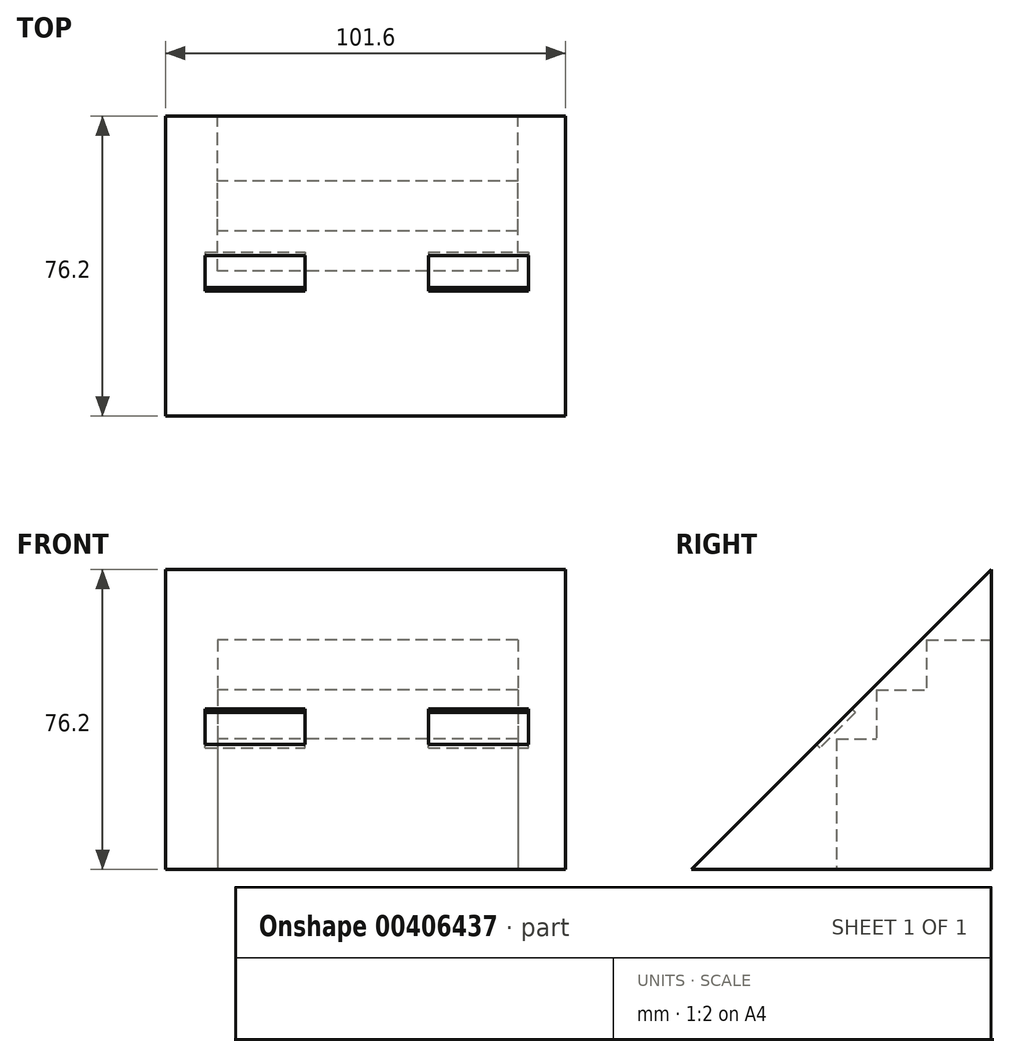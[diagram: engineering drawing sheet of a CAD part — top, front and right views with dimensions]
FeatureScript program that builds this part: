
annotation { "Feature Type Name" : "Feature", "Feature Type Description" : "" }
export const myFeature = defineFeature(function(context is Context, id is Id, definition is map)
    precondition{}
    {
        {
            var Q0;
            Q0=qCreatedBy(makeId("Right.planeOp"),FACE);
            var sketch = newSketch(context, id + "F0", { "sketchPlane" : qUnion([Q0])});
            skLineSegment(sketch, "E0.top", {"start": v(-48.38, -33.15) * mm, "end": v(27.82, -33.15) * mm});
            skLineSegment(sketch, "E0.right", {"start": v(27.82, 43.05) * mm, "end": v(27.82, -33.15) * mm});
            skLineSegment(sketch, "E1", {"start": v(27.82, 43.05) * mm, "end": v(-48.38, -33.15) * mm});
            skSolve(sketch);
        }
        {
            var Q0;
            Q0=makeQuery(id+"F0.imprint","IMPRINT",FACE,{"disambiguationData":[TD([[makeQuery(id+"F0.imprint","IMPRINT",EDGE,{"derivedFrom":sQuery(id+"F0.wireOp",EDGE,"E0.top")}),1.0]])]});
            extrude(context, id + "F1", {"entities" : qUnion([Q0]), "depth" : 101.6 * mm});
        }
        {
            var Q0;
            Q0=makeQuery(id+"F1.opExtrude","SWEPT_FACE",FACE,{"disambiguationData":[OSD([sQuery(id+"F0.wireOp",EDGE,"E1")])]});
            var sketch = newSketch(context, id + "F2", { "sketchPlane" : qUnion([Q0])});
            skLineSegment(sketch, "E2.bottom", {"start": v(10, 0) * mm, "end": v(35.4, 0) * mm});
            skLineSegment(sketch, "E2.top", {"start": v(10, -12.7) * mm, "end": v(35.4, -12.7) * mm});
            skLineSegment(sketch, "E2.left", {"start": v(10, 0) * mm, "end": v(10, -12.7) * mm});
            skLineSegment(sketch, "E2.right", {"start": v(35.4, 0) * mm, "end": v(35.4, -12.7) * mm});
            skLineSegment(sketch, "E3.bottom", {"start": v(66.77, 0) * mm, "end": v(92.17, 0) * mm});
            skLineSegment(sketch, "E3.top", {"start": v(66.77, -12.7) * mm, "end": v(92.17, -12.7) * mm});
            skLineSegment(sketch, "E3.left", {"start": v(66.77, 0) * mm, "end": v(66.77, -12.7) * mm});
            skLineSegment(sketch, "E3.right", {"start": v(92.17, 0) * mm, "end": v(92.17, -12.7) * mm});
            skSolve(sketch);
        }
        {
            var Q0;
            Q0=makeQuery(id+"F2.imprint","IMPRINT",FACE,{"disambiguationData":[TD([[makeQuery(id+"F2.imprint","IMPRINT",EDGE,{"derivedFrom":sQuery(id+"F2.wireOp",EDGE,"E2.bottom")}),-1.0]])]});
            var Q1;
            Q1=makeQuery(id+"F2.imprint","IMPRINT",FACE,{"disambiguationData":[TD([[makeQuery(id+"F2.imprint","IMPRINT",EDGE,{"derivedFrom":sQuery(id+"F2.wireOp",EDGE,"E3.bottom")}),-1.0]])]});
            extrude(context, id + "F3", {"entities" : qUnion([Q0, Q1]), "operationType" : NewBodyOperationType.REMOVE, "oppositeDirection" : true, "depth" : 1.27 * mm});
        }
        {
            var Q0;
            Q0=makeQuery(id+"F1.opExtrude","SWEPT_FACE",FACE,{"disambiguationData":[OSD([sQuery(id+"F0.wireOp",EDGE,"E0.right")])]});
            var sketch = newSketch(context, id + "F4", { "sketchPlane" : qUnion([Q0])});
            skLineSegment(sketch, "E4.bottom", {"start": v(-89.53, 25.2) * mm, "end": v(-13.19, 25.2) * mm});
            skLineSegment(sketch, "E4.top", {"start": v(-89.53, -33.15) * mm, "end": v(-13.19, -33.15) * mm});
            skLineSegment(sketch, "E4.left", {"start": v(-89.53, 25.2) * mm, "end": v(-89.53, -33.15) * mm});
            skLineSegment(sketch, "E4.right", {"start": v(-13.19, 25.2) * mm, "end": v(-13.19, -33.15) * mm});
            skLineSegment(sketch, "E5.bottom", {"start": v(-89.53, 12.97) * mm, "end": v(-13.19, 12.97) * mm});
            skLineSegment(sketch, "E5.left", {"start": v(-89.53, 12.97) * mm, "end": v(-89.53, -33.15) * mm});
            skLineSegment(sketch, "E5.right", {"start": v(-13.19, 12.97) * mm, "end": v(-13.19, -33.15) * mm});
            skLineSegment(sketch, "E6.bottom", {"start": v(-89.53, 0) * mm, "end": v(-13.19, 0) * mm});
            skLineSegment(sketch, "E6.left", {"start": v(-89.53, 0) * mm, "end": v(-89.53, -33.15) * mm});
            skLineSegment(sketch, "E6.right", {"start": v(-13.19, 0) * mm, "end": v(-13.19, -33.15) * mm});
            skLineSegment(sketch, "E7.bottom", {"start": v(-89.53, -10.1) * mm, "end": v(-13.19, -10.1) * mm});
            skLineSegment(sketch, "E7.left", {"start": v(-89.53, -10.1) * mm, "end": v(-89.53, -33.15) * mm});
            skLineSegment(sketch, "E7.right", {"start": v(-13.19, -10.1) * mm, "end": v(-13.19, -33.15) * mm});
            skLineSegment(sketch, "E8.bottom", {"start": v(-89.53, -21.62) * mm, "end": v(-13.19, -21.62) * mm});
            skLineSegment(sketch, "E8.left", {"start": v(-89.53, -21.62) * mm, "end": v(-89.53, -33.15) * mm});
            skLineSegment(sketch, "E8.right", {"start": v(-13.19, -21.62) * mm, "end": v(-13.19, -33.15) * mm});
            skSolve(sketch);
        }
        {
            var Q0;
            Q0=makeQuery(id+"F4.imprint","IMPRINT",FACE,{"disambiguationData":[TD([[makeQuery(id+"F4.imprint","IMPRINT",EDGE,{"derivedFrom":sQuery(id+"F4.wireOp",EDGE,"E4.bottom")}),-1.0]])]});
            var Q1;
            Q1=makeQuery(id+"F4.imprint","IMPRINT",FACE,{"disambiguationData":[TD([[makeQuery(id+"F4.imprint","IMPRINT",EDGE,{"derivedFrom":sQuery(id+"F4.wireOp",EDGE,"E5.bottom")}),-1.0]])]});
            var Q2;
            Q2=makeQuery(id+"F4.imprint","IMPRINT",FACE,{"disambiguationData":[TD([[makeQuery(id+"F4.imprint","IMPRINT",EDGE,{"derivedFrom":sQuery(id+"F4.wireOp",EDGE,"E6.bottom")}),-1.0]])]});
            var Q3;
            Q3=makeQuery(id+"F4.imprint","IMPRINT",FACE,{"disambiguationData":[TD([[makeQuery(id+"F4.imprint","IMPRINT",EDGE,{"derivedFrom":sQuery(id+"F4.wireOp",EDGE,"E7.bottom")}),-1.0]])]});
            var Q4;
            Q4=makeQuery(id+"F4.imprint","IMPRINT",FACE,{"disambiguationData":[TD([[makeQuery(id+"F4.imprint","IMPRINT",EDGE,{"derivedFrom":sQuery(id+"F4.wireOp",EDGE,"E8.bottom")}),-1.0]])]});
            extrude(context, id + "F5", {"entities" : qUnion([Q0, Q1, Q2, Q3, Q4]), "operationType" : NewBodyOperationType.REMOVE, "oppositeDirection" : true, "depth" : 16.5 * mm});
        }
        {
            var Q0;
            Q0=makeQuery(id+"F5.boolean.opBoolean","COPY",FACE,{"derivedFrom":makeQuery(id+"F5.opExtrude","CAP_FACE",FACE,{"disambiguationData":[OSD([sQuery(id+"F4.wireOp",EDGE,"E4.bottom"),sQuery(id+"F4.wireOp",EDGE,"E4.left"),sQuery(id+"F4.wireOp",EDGE,"E4.right"),sQuery(id+"F4.wireOp",EDGE,"E5.left"),sQuery(id+"F4.wireOp",EDGE,"E5.right"),sQuery(id+"F4.wireOp",EDGE,"E6.left"),sQuery(id+"F4.wireOp",EDGE,"E6.right"),sQuery(id+"F4.wireOp",EDGE,"E7.left"),sQuery(id+"F4.wireOp",EDGE,"E7.right"),sQuery(id+"F4.wireOp",EDGE,"E4.top"),sQuery(id+"F4.wireOp",EDGE,"E8.left"),sQuery(id+"F4.wireOp",EDGE,"E8.right")])],"isStart":false})});
            var sketch = newSketch(context, id + "F6", { "sketchPlane" : qUnion([Q0])});
            skLineSegment(sketch, "E9", {"start": v(-89.53, 12.48) * mm, "end": v(-13.19, 12.48) * mm});
            skSolve(sketch);
        }
        {
            var Q0;
            {var subQ0=sQuery(id+"F6.wireOp",EDGE,"E9");Q0=makeQuery(id+"F6.imprint","IMPRINT",FACE,{"disambiguationData":[TD([[makeQuery(id+"F6.imprint","IMPRINT",EDGE,{"derivedFrom":subQ0}),-1.0]])]});}
            extrude(context, id + "F7", {"entities" : qUnion([Q0]), "operationType" : NewBodyOperationType.REMOVE, "oppositeDirection" : true, "depth" : 12.7 * mm});
        }
        {
            var Q0;
            Q0=makeQuery(id+"F7.boolean.opBoolean","COPY",FACE,{"derivedFrom":makeQuery(id+"F7.opExtrude","CAP_FACE",FACE,{"disambiguationData":[OSD([sQuery(id+"F4.wireOp",EDGE,"E4.left"),sQuery(id+"F4.wireOp",EDGE,"E4.right"),sQuery(id+"F4.wireOp",EDGE,"E5.left"),sQuery(id+"F4.wireOp",EDGE,"E5.right"),sQuery(id+"F4.wireOp",EDGE,"E6.left"),sQuery(id+"F4.wireOp",EDGE,"E6.right"),sQuery(id+"F4.wireOp",EDGE,"E7.left"),sQuery(id+"F4.wireOp",EDGE,"E7.right"),sQuery(id+"F4.wireOp",EDGE,"E4.top"),sQuery(id+"F4.wireOp",EDGE,"E8.left"),sQuery(id+"F4.wireOp",EDGE,"E8.right"),sQuery(id+"F6.wireOp",EDGE,"E9")])],"isStart":false})});
            var sketch = newSketch(context, id + "F8", { "sketchPlane" : qUnion([Q0])});
            skLineSegment(sketch, "E10", {"start": v(-89.53, 0) * mm, "end": v(-13.19, 0) * mm});
            skSolve(sketch);
        }
        {
            var Q0;
            {var subQ0=sQuery(id+"F8.wireOp",EDGE,"E10");Q0=makeQuery(id+"F8.imprint","IMPRINT",FACE,{"disambiguationData":[TD([[makeQuery(id+"F8.imprint","IMPRINT",EDGE,{"derivedFrom":subQ0}),-1.0]])]});}
            extrude(context, id + "F9", {"entities" : qUnion([Q0]), "operationType" : NewBodyOperationType.REMOVE, "oppositeDirection" : true, "depth" : 10.16 * mm});
        }
    });
